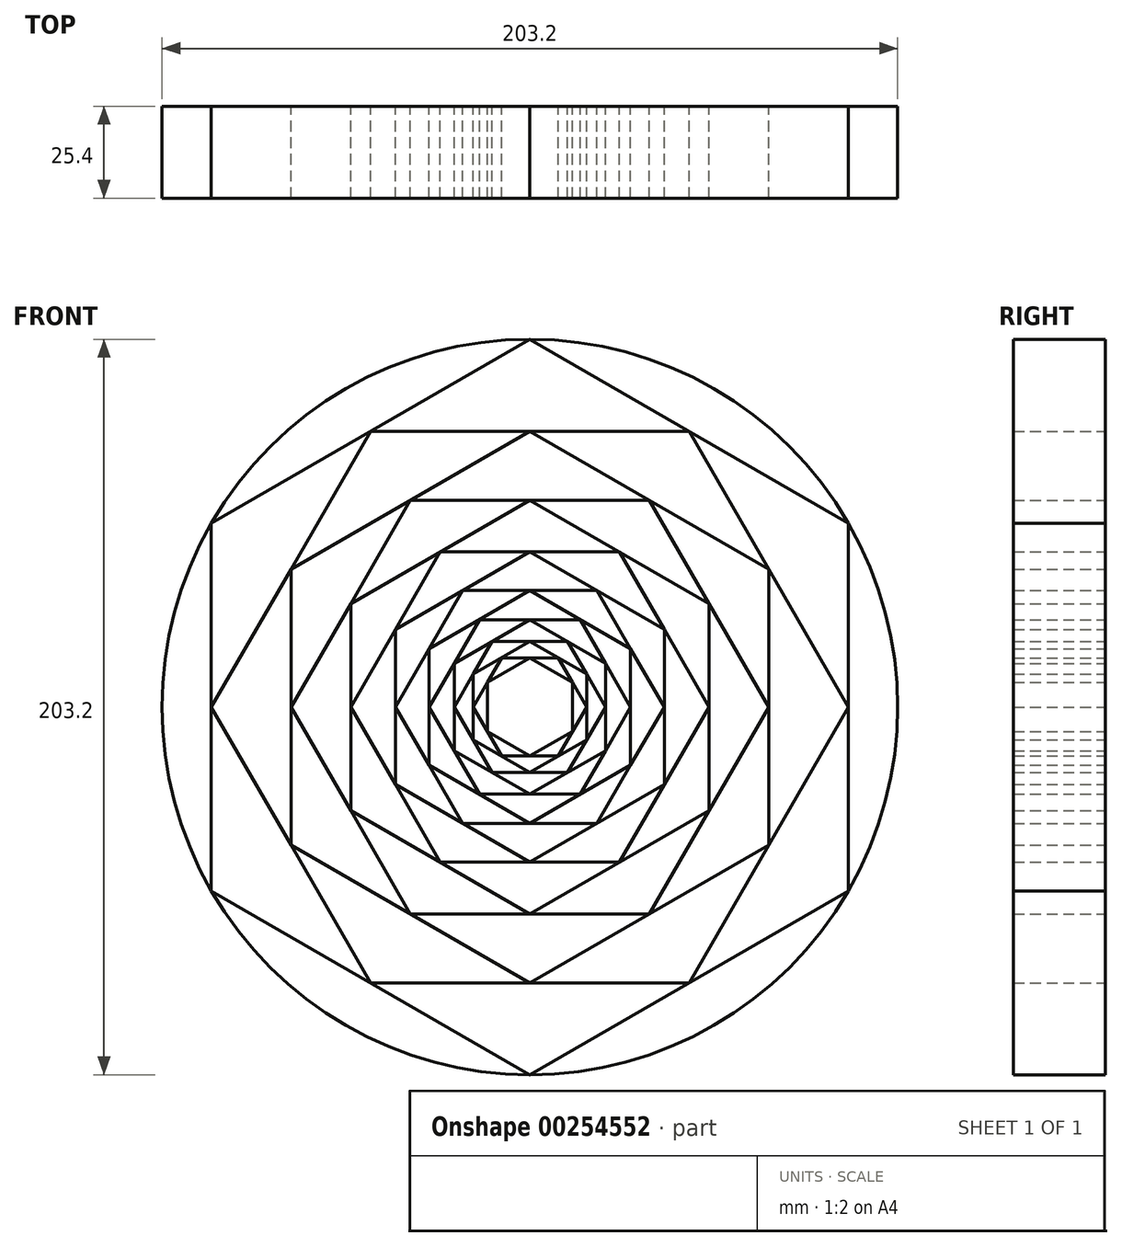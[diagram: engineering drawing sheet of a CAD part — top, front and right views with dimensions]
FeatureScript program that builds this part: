
annotation { "Feature Type Name" : "Feature", "Feature Type Description" : "" }
export const myFeature = defineFeature(function(context is Context, id is Id, definition is map)
    precondition{}
    {
        {
            var Q0;
            Q0=qCreatedBy(makeId("Front.planeOp"),FACE);
            var sketch = newSketch(context, id + "F0", { "sketchPlane" : qUnion([Q0])});
            skCircle(sketch, "E0", {"center": v(0, 0) * mm, "radius": 101.6 * mm});
            skCircle(sketch, "E1.cCircle", {"center": v(0, 0) * mm, "radius": 101.6 * mm, "construction": true});
            skLineSegment(sketch, "E1.0", {"start": v(0, 101.6) * mm, "end": v(87.99, 50.8) * mm});
            skLineSegment(sketch, "E1.1", {"start": v(87.99, 50.8) * mm, "end": v(87.99, -50.8) * mm});
            skLineSegment(sketch, "E1.2", {"start": v(87.99, -50.8) * mm, "end": v(0, -101.6) * mm});
            skLineSegment(sketch, "E1.3", {"start": v(0, -101.6) * mm, "end": v(-87.99, -50.8) * mm});
            skLineSegment(sketch, "E1.4", {"start": v(-87.99, -50.8) * mm, "end": v(-87.99, 50.8) * mm});
            skLineSegment(sketch, "E1.5", {"start": v(-87.99, 50.8) * mm, "end": v(0, 101.6) * mm});
            skCircle(sketch, "E2.cCircle", {"center": v(0, 0) * mm, "radius": 87.99 * mm, "construction": true});
            skLineSegment(sketch, "E2.0", {"start": v(-87.99, 0) * mm, "end": v(-44, 76.2) * mm});
            skLineSegment(sketch, "E2.1", {"start": v(-44, 76.2) * mm, "end": v(44, 76.2) * mm});
            skLineSegment(sketch, "E2.2", {"start": v(44, 76.2) * mm, "end": v(87.99, 0) * mm});
            skLineSegment(sketch, "E2.3", {"start": v(87.99, 0) * mm, "end": v(44, -76.2) * mm});
            skLineSegment(sketch, "E2.4", {"start": v(44, -76.2) * mm, "end": v(-44, -76.2) * mm});
            skLineSegment(sketch, "E2.5", {"start": v(-44, -76.2) * mm, "end": v(-87.99, 0) * mm});
            skCircle(sketch, "E3.cCircle", {"center": v(0, 0) * mm, "radius": 76.2 * mm, "construction": true});
            skLineSegment(sketch, "E3.0", {"start": v(0, 76.2) * mm, "end": v(66, 38.1) * mm});
            skLineSegment(sketch, "E3.1", {"start": v(66, 38.1) * mm, "end": v(66, -38.1) * mm});
            skLineSegment(sketch, "E3.2", {"start": v(66, -38.1) * mm, "end": v(0, -76.2) * mm});
            skLineSegment(sketch, "E3.3", {"start": v(0, -76.2) * mm, "end": v(-66, -38.1) * mm});
            skLineSegment(sketch, "E3.4", {"start": v(-66, -38.1) * mm, "end": v(-66, 38.1) * mm});
            skLineSegment(sketch, "E3.5", {"start": v(-66, 38.1) * mm, "end": v(0, 76.2) * mm});
            skCircle(sketch, "E4.cCircle", {"center": v(0, 0) * mm, "radius": 66 * mm, "construction": true});
            skLineSegment(sketch, "E4.0", {"start": v(66, 0) * mm, "end": v(33, -57.15) * mm});
            skLineSegment(sketch, "E4.1", {"start": v(33, -57.15) * mm, "end": v(-33, -57.15) * mm});
            skLineSegment(sketch, "E4.2", {"start": v(-33, -57.15) * mm, "end": v(-66, 0) * mm});
            skLineSegment(sketch, "E4.3", {"start": v(-66, 0) * mm, "end": v(-33, 57.15) * mm});
            skLineSegment(sketch, "E4.4", {"start": v(-33, 57.15) * mm, "end": v(33, 57.15) * mm});
            skLineSegment(sketch, "E4.5", {"start": v(33, 57.15) * mm, "end": v(66, 0) * mm});
            skCircle(sketch, "E5.cCircle", {"center": v(0, 0) * mm, "radius": 57.15 * mm, "construction": true});
            skLineSegment(sketch, "E5.0", {"start": v(0, 57.15) * mm, "end": v(49.5, 28.58) * mm});
            skLineSegment(sketch, "E5.1", {"start": v(49.5, 28.58) * mm, "end": v(49.5, -28.57) * mm});
            skLineSegment(sketch, "E5.2", {"start": v(49.5, -28.57) * mm, "end": v(0, -57.15) * mm});
            skLineSegment(sketch, "E5.3", {"start": v(0, -57.15) * mm, "end": v(-49.5, -28.58) * mm});
            skLineSegment(sketch, "E5.4", {"start": v(-49.5, -28.58) * mm, "end": v(-49.5, 28.57) * mm});
            skLineSegment(sketch, "E5.5", {"start": v(-49.5, 28.57) * mm, "end": v(0, 57.15) * mm});
            skCircle(sketch, "E6.cCircle", {"center": v(0, 0) * mm, "radius": 49.5 * mm, "construction": true});
            skLineSegment(sketch, "E6.0", {"start": v(49.5, 0) * mm, "end": v(24.75, -42.86) * mm});
            skLineSegment(sketch, "E6.1", {"start": v(24.75, -42.86) * mm, "end": v(-24.75, -42.86) * mm});
            skLineSegment(sketch, "E6.2", {"start": v(-24.75, -42.86) * mm, "end": v(-49.5, 0) * mm});
            skLineSegment(sketch, "E6.3", {"start": v(-49.5, 0) * mm, "end": v(-24.75, 42.86) * mm});
            skLineSegment(sketch, "E6.4", {"start": v(-24.75, 42.86) * mm, "end": v(24.75, 42.86) * mm});
            skLineSegment(sketch, "E6.5", {"start": v(24.75, 42.86) * mm, "end": v(49.5, 0) * mm});
            skCircle(sketch, "E7.cCircle", {"center": v(0, 0) * mm, "radius": 42.86 * mm, "construction": true});
            skLineSegment(sketch, "E7.0", {"start": v(0, 42.86) * mm, "end": v(37.12, 21.43) * mm});
            skLineSegment(sketch, "E7.1", {"start": v(37.12, 21.43) * mm, "end": v(37.12, -21.43) * mm});
            skLineSegment(sketch, "E7.2", {"start": v(37.12, -21.43) * mm, "end": v(0, -42.86) * mm});
            skLineSegment(sketch, "E7.3", {"start": v(0, -42.86) * mm, "end": v(-37.12, -21.43) * mm});
            skLineSegment(sketch, "E7.4", {"start": v(-37.12, -21.43) * mm, "end": v(-37.12, 21.43) * mm});
            skLineSegment(sketch, "E7.5", {"start": v(-37.12, 21.43) * mm, "end": v(0, 42.86) * mm});
            skCircle(sketch, "E8.cCircle", {"center": v(0, 0) * mm, "radius": 37.12 * mm, "construction": true});
            skLineSegment(sketch, "E8.0", {"start": v(37.12, 0) * mm, "end": v(18.56, -32.15) * mm});
            skLineSegment(sketch, "E8.1", {"start": v(18.56, -32.15) * mm, "end": v(-18.56, -32.15) * mm});
            skLineSegment(sketch, "E8.2", {"start": v(-18.56, -32.15) * mm, "end": v(-37.12, 0) * mm});
            skLineSegment(sketch, "E8.3", {"start": v(-37.12, 0) * mm, "end": v(-18.56, 32.15) * mm});
            skLineSegment(sketch, "E8.4", {"start": v(-18.56, 32.15) * mm, "end": v(18.56, 32.15) * mm});
            skLineSegment(sketch, "E8.5", {"start": v(18.56, 32.15) * mm, "end": v(37.12, 0) * mm});
            skCircle(sketch, "E9.cCircle", {"center": v(0, 0) * mm, "radius": 32.15 * mm, "construction": true});
            skLineSegment(sketch, "E9.0", {"start": v(0, 32.15) * mm, "end": v(27.84, 16.07) * mm});
            skLineSegment(sketch, "E9.1", {"start": v(27.84, 16.07) * mm, "end": v(27.84, -16.07) * mm});
            skLineSegment(sketch, "E9.2", {"start": v(27.84, -16.07) * mm, "end": v(0, -32.15) * mm});
            skLineSegment(sketch, "E9.3", {"start": v(0, -32.15) * mm, "end": v(-27.84, -16.07) * mm});
            skLineSegment(sketch, "E9.4", {"start": v(-27.84, -16.07) * mm, "end": v(-27.84, 16.07) * mm});
            skLineSegment(sketch, "E9.5", {"start": v(-27.84, 16.07) * mm, "end": v(0, 32.15) * mm});
            skCircle(sketch, "E10.cCircle", {"center": v(0, 0) * mm, "radius": 27.84 * mm, "construction": true});
            skLineSegment(sketch, "E10.0", {"start": v(27.84, 0) * mm, "end": v(13.92, -24.11) * mm});
            skLineSegment(sketch, "E10.1", {"start": v(13.92, -24.11) * mm, "end": v(-13.92, -24.11) * mm});
            skLineSegment(sketch, "E10.2", {"start": v(-13.92, -24.11) * mm, "end": v(-27.84, 0) * mm});
            skLineSegment(sketch, "E10.3", {"start": v(-27.84, 0) * mm, "end": v(-13.92, 24.11) * mm});
            skLineSegment(sketch, "E10.4", {"start": v(-13.92, 24.11) * mm, "end": v(13.92, 24.11) * mm});
            skLineSegment(sketch, "E10.5", {"start": v(13.92, 24.11) * mm, "end": v(27.84, 0) * mm});
            skCircle(sketch, "E11.cCircle", {"center": v(0, 0) * mm, "radius": 24.11 * mm, "construction": true});
            skLineSegment(sketch, "E11.0", {"start": v(0, 24.11) * mm, "end": v(20.88, 12.06) * mm});
            skLineSegment(sketch, "E11.1", {"start": v(20.88, 12.06) * mm, "end": v(20.88, -12.06) * mm});
            skLineSegment(sketch, "E11.2", {"start": v(20.88, -12.06) * mm, "end": v(0, -24.11) * mm});
            skLineSegment(sketch, "E11.3", {"start": v(0, -24.11) * mm, "end": v(-20.88, -12.06) * mm});
            skLineSegment(sketch, "E11.4", {"start": v(-20.88, -12.06) * mm, "end": v(-20.88, 12.06) * mm});
            skLineSegment(sketch, "E11.5", {"start": v(-20.88, 12.06) * mm, "end": v(0, 24.11) * mm});
            skCircle(sketch, "E12.cCircle", {"center": v(0, 0) * mm, "radius": 20.88 * mm, "construction": true});
            skLineSegment(sketch, "E13.0", {"start": v(20.88, 0) * mm, "end": v(10.44, -18.08) * mm});
            skLineSegment(sketch, "E13.1", {"start": v(10.44, -18.08) * mm, "end": v(-10.44, -18.08) * mm});
            skLineSegment(sketch, "E13.2", {"start": v(-10.44, -18.08) * mm, "end": v(-20.88, 0) * mm});
            skLineSegment(sketch, "E13.3", {"start": v(-20.88, 0) * mm, "end": v(-10.44, 18.08) * mm});
            skLineSegment(sketch, "E13.4", {"start": v(-10.44, 18.08) * mm, "end": v(10.44, 18.08) * mm});
            skLineSegment(sketch, "E13.5", {"start": v(10.44, 18.08) * mm, "end": v(20.88, 0) * mm});
            skCircle(sketch, "E14.cCircle", {"center": v(0, 0) * mm, "radius": 18.08 * mm, "construction": true});
            skLineSegment(sketch, "E14.0", {"start": v(0, 18.08) * mm, "end": v(15.66, 9.04) * mm});
            skLineSegment(sketch, "E14.1", {"start": v(15.66, 9.04) * mm, "end": v(15.66, -9.04) * mm});
            skLineSegment(sketch, "E14.2", {"start": v(15.66, -9.04) * mm, "end": v(0, -18.08) * mm});
            skLineSegment(sketch, "E14.3", {"start": v(0, -18.08) * mm, "end": v(-15.66, -9.04) * mm});
            skLineSegment(sketch, "E14.4", {"start": v(-15.66, -9.04) * mm, "end": v(-15.66, 9.04) * mm});
            skLineSegment(sketch, "E14.5", {"start": v(-15.66, 9.04) * mm, "end": v(0, 18.08) * mm});
            skCircle(sketch, "E15.cCircle", {"center": v(0, 0) * mm, "radius": 15.66 * mm, "construction": true});
            skLineSegment(sketch, "E15.0", {"start": v(15.66, 0) * mm, "end": v(7.83, -13.56) * mm});
            skLineSegment(sketch, "E15.1", {"start": v(7.83, -13.56) * mm, "end": v(-7.83, -13.56) * mm});
            skLineSegment(sketch, "E15.2", {"start": v(-7.83, -13.56) * mm, "end": v(-15.66, 0) * mm});
            skLineSegment(sketch, "E15.3", {"start": v(-15.66, 0) * mm, "end": v(-7.83, 13.56) * mm});
            skLineSegment(sketch, "E15.4", {"start": v(-7.83, 13.56) * mm, "end": v(7.83, 13.56) * mm});
            skLineSegment(sketch, "E15.5", {"start": v(7.83, 13.56) * mm, "end": v(15.66, 0) * mm});
            skCircle(sketch, "E16.cCircle", {"center": v(0, 0) * mm, "radius": 13.56 * mm, "construction": true});
            skLineSegment(sketch, "E16.0", {"start": v(0, 13.56) * mm, "end": v(11.75, 6.78) * mm});
            skLineSegment(sketch, "E16.1", {"start": v(11.75, 6.78) * mm, "end": v(11.75, -6.78) * mm});
            skLineSegment(sketch, "E16.2", {"start": v(11.75, -6.78) * mm, "end": v(0, -13.56) * mm});
            skLineSegment(sketch, "E16.3", {"start": v(0, -13.56) * mm, "end": v(-11.75, -6.78) * mm});
            skLineSegment(sketch, "E16.4", {"start": v(-11.75, -6.78) * mm, "end": v(-11.75, 6.78) * mm});
            skLineSegment(sketch, "E16.5", {"start": v(-11.75, 6.78) * mm, "end": v(0, 13.56) * mm});
            skCircle(sketch, "E17.cCircle", {"center": v(0, 0) * mm, "radius": 11.75 * mm, "construction": true});
            skLineSegment(sketch, "E17.0", {"start": v(11.75, 0) * mm, "end": v(5.87, -10.17) * mm});
            skLineSegment(sketch, "E17.1", {"start": v(5.87, -10.17) * mm, "end": v(-5.87, -10.17) * mm});
            skLineSegment(sketch, "E17.2", {"start": v(-5.87, -10.17) * mm, "end": v(-11.75, 0) * mm});
            skLineSegment(sketch, "E17.3", {"start": v(-11.75, 0) * mm, "end": v(-5.87, 10.17) * mm});
            skLineSegment(sketch, "E17.4", {"start": v(-5.87, 10.17) * mm, "end": v(5.87, 10.17) * mm});
            skLineSegment(sketch, "E17.5", {"start": v(5.87, 10.17) * mm, "end": v(11.75, 0) * mm});
            skSolve(sketch);
        }
        {
            var Q0;
            {var subQ0=sQuery(id+"F0.wireOp",EDGE,"E1.5");var subQ1=sQuery(id+"F0.wireOp",EDGE,"E0");var subQ2=makeQuery(id+"F0.imprint","INTERSECT",VERTEX,{"derivedFrom":[subQ1,sQuery(id+"F0.wireOp",EDGE,"E1.0"),subQ0]});Q0=makeQuery(id+"F0.imprint","IMPRINT",FACE,{"disambiguationData":[TD([[makeQuery(id+"F0.imprint","IMPRINT",EDGE,{"disambiguationData":[TD([[subQ2,-1.0]])],"derivedFrom":subQ1}),1.0]])]});}
            var Q1;
            {var subQ0=sQuery(id+"F0.wireOp",EDGE,"E1.0");var subQ1=sQuery(id+"F0.wireOp",EDGE,"E0");var subQ2=makeQuery(id+"F0.imprint","INTERSECT",VERTEX,{"derivedFrom":[subQ1,subQ0,sQuery(id+"F0.wireOp",EDGE,"E1.5")]});Q1=makeQuery(id+"F0.imprint","IMPRINT",FACE,{"disambiguationData":[TD([[makeQuery(id+"F0.imprint","IMPRINT",EDGE,{"disambiguationData":[TD([[subQ2,1.0]])],"derivedFrom":subQ1}),1.0]])]});}
            var Q2;
            {var subQ0=sQuery(id+"F0.wireOp",EDGE,"E1.1");var subQ1=sQuery(id+"F0.wireOp",EDGE,"E0");var subQ2=makeQuery(id+"F0.imprint","INTERSECT",VERTEX,{"derivedFrom":[subQ1,sQuery(id+"F0.wireOp",EDGE,"E1.0"),subQ0]});Q2=makeQuery(id+"F0.imprint","IMPRINT",FACE,{"disambiguationData":[TD([[makeQuery(id+"F0.imprint","IMPRINT",EDGE,{"disambiguationData":[TD([[subQ2,1.0]])],"derivedFrom":subQ1}),1.0]])]});}
            var Q3;
            {var subQ0=sQuery(id+"F0.wireOp",EDGE,"E1.2");var subQ1=sQuery(id+"F0.wireOp",EDGE,"E0");var subQ2=makeQuery(id+"F0.imprint","INTERSECT",VERTEX,{"derivedFrom":[subQ1,sQuery(id+"F0.wireOp",EDGE,"E1.1"),subQ0]});Q3=makeQuery(id+"F0.imprint","IMPRINT",FACE,{"disambiguationData":[TD([[makeQuery(id+"F0.imprint","IMPRINT",EDGE,{"disambiguationData":[TD([[subQ2,1.0]])],"derivedFrom":subQ1}),1.0]])]});}
            var Q4;
            {var subQ0=sQuery(id+"F0.wireOp",EDGE,"E1.3");var subQ1=sQuery(id+"F0.wireOp",EDGE,"E0");var subQ2=makeQuery(id+"F0.imprint","INTERSECT",VERTEX,{"derivedFrom":[subQ1,sQuery(id+"F0.wireOp",EDGE,"E1.2"),subQ0]});Q4=makeQuery(id+"F0.imprint","IMPRINT",FACE,{"disambiguationData":[TD([[makeQuery(id+"F0.imprint","IMPRINT",EDGE,{"disambiguationData":[TD([[subQ2,1.0]])],"derivedFrom":subQ1}),1.0]])]});}
            var Q5;
            {var subQ0=sQuery(id+"F0.wireOp",EDGE,"E1.4");var subQ1=sQuery(id+"F0.wireOp",EDGE,"E0");var subQ2=makeQuery(id+"F0.imprint","INTERSECT",VERTEX,{"derivedFrom":[subQ1,sQuery(id+"F0.wireOp",EDGE,"E1.3"),subQ0]});Q5=makeQuery(id+"F0.imprint","IMPRINT",FACE,{"disambiguationData":[TD([[makeQuery(id+"F0.imprint","IMPRINT",EDGE,{"disambiguationData":[TD([[subQ2,1.0]])],"derivedFrom":subQ1}),1.0]])]});}
            var Q6;
            {var subQ0=sQuery(id+"F0.wireOp",EDGE,"E2.5");var subQ1=sQuery(id+"F0.wireOp",EDGE,"E2.4");var subQ2=makeQuery(id+"F0.imprint","INTERSECT",VERTEX,{"derivedFrom":[sQuery(id+"F0.wireOp",EDGE,"E1.3"),subQ1,subQ0]});Q6=makeQuery(id+"F0.imprint","IMPRINT",FACE,{"disambiguationData":[TD([[makeQuery(id+"F0.imprint","IMPRINT",EDGE,{"disambiguationData":[TD([[subQ2,1.0]])],"derivedFrom":subQ1}),-1.0]])]});}
            var Q7;
            {var subQ0=sQuery(id+"F0.wireOp",EDGE,"E2.4");var subQ1=sQuery(id+"F0.wireOp",EDGE,"E2.3");var subQ2=makeQuery(id+"F0.imprint","INTERSECT",VERTEX,{"derivedFrom":[sQuery(id+"F0.wireOp",EDGE,"E1.2"),subQ1,subQ0]});Q7=makeQuery(id+"F0.imprint","IMPRINT",FACE,{"disambiguationData":[TD([[makeQuery(id+"F0.imprint","IMPRINT",EDGE,{"disambiguationData":[TD([[subQ2,1.0]])],"derivedFrom":subQ1}),-1.0]])]});}
            var Q8;
            {var subQ0=sQuery(id+"F0.wireOp",EDGE,"E2.3");var subQ1=sQuery(id+"F0.wireOp",EDGE,"E2.2");var subQ2=makeQuery(id+"F0.imprint","INTERSECT",VERTEX,{"derivedFrom":[sQuery(id+"F0.wireOp",EDGE,"E1.1"),subQ1,subQ0]});Q8=makeQuery(id+"F0.imprint","IMPRINT",FACE,{"disambiguationData":[TD([[makeQuery(id+"F0.imprint","IMPRINT",EDGE,{"disambiguationData":[TD([[subQ2,1.0]])],"derivedFrom":subQ1}),-1.0]])]});}
            var Q9;
            {var subQ0=sQuery(id+"F0.wireOp",EDGE,"E2.2");var subQ1=sQuery(id+"F0.wireOp",EDGE,"E2.1");var subQ2=makeQuery(id+"F0.imprint","INTERSECT",VERTEX,{"derivedFrom":[sQuery(id+"F0.wireOp",EDGE,"E1.0"),subQ1,subQ0]});Q9=makeQuery(id+"F0.imprint","IMPRINT",FACE,{"disambiguationData":[TD([[makeQuery(id+"F0.imprint","IMPRINT",EDGE,{"disambiguationData":[TD([[subQ2,1.0]])],"derivedFrom":subQ1}),-1.0]])]});}
            var Q10;
            {var subQ0=sQuery(id+"F0.wireOp",EDGE,"E2.1");var subQ1=sQuery(id+"F0.wireOp",EDGE,"E2.0");var subQ2=makeQuery(id+"F0.imprint","INTERSECT",VERTEX,{"derivedFrom":[sQuery(id+"F0.wireOp",EDGE,"E1.5"),subQ1,subQ0]});Q10=makeQuery(id+"F0.imprint","IMPRINT",FACE,{"disambiguationData":[TD([[makeQuery(id+"F0.imprint","IMPRINT",EDGE,{"disambiguationData":[TD([[subQ2,1.0]])],"derivedFrom":subQ1}),-1.0]])]});}
            var Q11;
            {var subQ0=sQuery(id+"F0.wireOp",EDGE,"E2.5");var subQ1=sQuery(id+"F0.wireOp",EDGE,"E2.0");var subQ2=makeQuery(id+"F0.imprint","INTERSECT",VERTEX,{"derivedFrom":[sQuery(id+"F0.wireOp",EDGE,"E1.4"),subQ1,subQ0]});Q11=makeQuery(id+"F0.imprint","IMPRINT",FACE,{"disambiguationData":[TD([[makeQuery(id+"F0.imprint","IMPRINT",EDGE,{"disambiguationData":[TD([[subQ2,-1.0]])],"derivedFrom":subQ1}),-1.0]])]});}
            var Q12;
            {var subQ0=sQuery(id+"F0.wireOp",EDGE,"E4.3");var subQ1=sQuery(id+"F0.wireOp",EDGE,"E4.2");var subQ2=makeQuery(id+"F0.imprint","INTERSECT",VERTEX,{"derivedFrom":[sQuery(id+"F0.wireOp",EDGE,"E3.4"),subQ1,subQ0]});Q12=makeQuery(id+"F0.imprint","IMPRINT",FACE,{"disambiguationData":[TD([[makeQuery(id+"F0.imprint","IMPRINT",EDGE,{"disambiguationData":[TD([[subQ2,1.0]])],"derivedFrom":subQ1}),-1.0]])]});}
            var Q13;
            {var subQ0=sQuery(id+"F0.wireOp",EDGE,"E4.2");var subQ1=sQuery(id+"F0.wireOp",EDGE,"E4.1");var subQ2=makeQuery(id+"F0.imprint","INTERSECT",VERTEX,{"derivedFrom":[sQuery(id+"F0.wireOp",EDGE,"E3.3"),subQ1,subQ0]});Q13=makeQuery(id+"F0.imprint","IMPRINT",FACE,{"disambiguationData":[TD([[makeQuery(id+"F0.imprint","IMPRINT",EDGE,{"disambiguationData":[TD([[subQ2,1.0]])],"derivedFrom":subQ1}),-1.0]])]});}
            var Q14;
            {var subQ0=sQuery(id+"F0.wireOp",EDGE,"E4.1");var subQ1=sQuery(id+"F0.wireOp",EDGE,"E4.0");var subQ2=makeQuery(id+"F0.imprint","INTERSECT",VERTEX,{"derivedFrom":[sQuery(id+"F0.wireOp",EDGE,"E3.2"),subQ1,subQ0]});Q14=makeQuery(id+"F0.imprint","IMPRINT",FACE,{"disambiguationData":[TD([[makeQuery(id+"F0.imprint","IMPRINT",EDGE,{"disambiguationData":[TD([[subQ2,1.0]])],"derivedFrom":subQ1}),-1.0]])]});}
            var Q15;
            {var subQ0=sQuery(id+"F0.wireOp",EDGE,"E4.5");var subQ1=sQuery(id+"F0.wireOp",EDGE,"E4.0");var subQ2=makeQuery(id+"F0.imprint","INTERSECT",VERTEX,{"derivedFrom":[sQuery(id+"F0.wireOp",EDGE,"E3.1"),subQ1,subQ0]});Q15=makeQuery(id+"F0.imprint","IMPRINT",FACE,{"disambiguationData":[TD([[makeQuery(id+"F0.imprint","IMPRINT",EDGE,{"disambiguationData":[TD([[subQ2,-1.0]])],"derivedFrom":subQ1}),-1.0]])]});}
            var Q16;
            {var subQ0=sQuery(id+"F0.wireOp",EDGE,"E4.5");var subQ1=sQuery(id+"F0.wireOp",EDGE,"E4.4");var subQ2=makeQuery(id+"F0.imprint","INTERSECT",VERTEX,{"derivedFrom":[sQuery(id+"F0.wireOp",EDGE,"E3.0"),subQ1,subQ0]});Q16=makeQuery(id+"F0.imprint","IMPRINT",FACE,{"disambiguationData":[TD([[makeQuery(id+"F0.imprint","IMPRINT",EDGE,{"disambiguationData":[TD([[subQ2,1.0]])],"derivedFrom":subQ1}),-1.0]])]});}
            var Q17;
            {var subQ0=sQuery(id+"F0.wireOp",EDGE,"E4.4");var subQ1=sQuery(id+"F0.wireOp",EDGE,"E4.3");var subQ2=makeQuery(id+"F0.imprint","INTERSECT",VERTEX,{"derivedFrom":[sQuery(id+"F0.wireOp",EDGE,"E3.5"),subQ1,subQ0]});Q17=makeQuery(id+"F0.imprint","IMPRINT",FACE,{"disambiguationData":[TD([[makeQuery(id+"F0.imprint","IMPRINT",EDGE,{"disambiguationData":[TD([[subQ2,1.0]])],"derivedFrom":subQ1}),-1.0]])]});}
            var Q18;
            {var subQ0=sQuery(id+"F0.wireOp",EDGE,"E6.4");var subQ1=sQuery(id+"F0.wireOp",EDGE,"E6.3");var subQ2=makeQuery(id+"F0.imprint","INTERSECT",VERTEX,{"derivedFrom":[sQuery(id+"F0.wireOp",EDGE,"E5.5"),subQ1,subQ0]});Q18=makeQuery(id+"F0.imprint","IMPRINT",FACE,{"disambiguationData":[TD([[makeQuery(id+"F0.imprint","IMPRINT",EDGE,{"disambiguationData":[TD([[subQ2,1.0]])],"derivedFrom":subQ1}),-1.0]])]});}
            var Q19;
            {var subQ0=sQuery(id+"F0.wireOp",EDGE,"E6.3");var subQ1=sQuery(id+"F0.wireOp",EDGE,"E6.2");var subQ2=makeQuery(id+"F0.imprint","INTERSECT",VERTEX,{"derivedFrom":[sQuery(id+"F0.wireOp",EDGE,"E5.4"),subQ1,subQ0]});Q19=makeQuery(id+"F0.imprint","IMPRINT",FACE,{"disambiguationData":[TD([[makeQuery(id+"F0.imprint","IMPRINT",EDGE,{"disambiguationData":[TD([[subQ2,1.0]])],"derivedFrom":subQ1}),-1.0]])]});}
            var Q20;
            {var subQ0=sQuery(id+"F0.wireOp",EDGE,"E6.2");var subQ1=sQuery(id+"F0.wireOp",EDGE,"E6.1");var subQ2=makeQuery(id+"F0.imprint","INTERSECT",VERTEX,{"derivedFrom":[sQuery(id+"F0.wireOp",EDGE,"E5.3"),subQ1,subQ0]});Q20=makeQuery(id+"F0.imprint","IMPRINT",FACE,{"disambiguationData":[TD([[makeQuery(id+"F0.imprint","IMPRINT",EDGE,{"disambiguationData":[TD([[subQ2,1.0]])],"derivedFrom":subQ1}),-1.0]])]});}
            var Q21;
            {var subQ0=sQuery(id+"F0.wireOp",EDGE,"E6.1");var subQ1=sQuery(id+"F0.wireOp",EDGE,"E6.0");var subQ2=makeQuery(id+"F0.imprint","INTERSECT",VERTEX,{"derivedFrom":[sQuery(id+"F0.wireOp",EDGE,"E5.2"),subQ1,subQ0]});Q21=makeQuery(id+"F0.imprint","IMPRINT",FACE,{"disambiguationData":[TD([[makeQuery(id+"F0.imprint","IMPRINT",EDGE,{"disambiguationData":[TD([[subQ2,1.0]])],"derivedFrom":subQ1}),-1.0]])]});}
            var Q22;
            {var subQ0=sQuery(id+"F0.wireOp",EDGE,"E6.5");var subQ1=sQuery(id+"F0.wireOp",EDGE,"E6.0");var subQ2=makeQuery(id+"F0.imprint","INTERSECT",VERTEX,{"derivedFrom":[sQuery(id+"F0.wireOp",EDGE,"E5.1"),subQ1,subQ0]});Q22=makeQuery(id+"F0.imprint","IMPRINT",FACE,{"disambiguationData":[TD([[makeQuery(id+"F0.imprint","IMPRINT",EDGE,{"disambiguationData":[TD([[subQ2,-1.0]])],"derivedFrom":subQ1}),-1.0]])]});}
            var Q23;
            {var subQ0=sQuery(id+"F0.wireOp",EDGE,"E6.5");var subQ1=sQuery(id+"F0.wireOp",EDGE,"E6.4");var subQ2=makeQuery(id+"F0.imprint","INTERSECT",VERTEX,{"derivedFrom":[sQuery(id+"F0.wireOp",EDGE,"E5.0"),subQ1,subQ0]});Q23=makeQuery(id+"F0.imprint","IMPRINT",FACE,{"disambiguationData":[TD([[makeQuery(id+"F0.imprint","IMPRINT",EDGE,{"disambiguationData":[TD([[subQ2,1.0]])],"derivedFrom":subQ1}),-1.0]])]});}
            var Q24;
            {var subQ0=sQuery(id+"F0.wireOp",EDGE,"E8.5");var subQ1=sQuery(id+"F0.wireOp",EDGE,"E8.4");var subQ2=makeQuery(id+"F0.imprint","INTERSECT",VERTEX,{"derivedFrom":[sQuery(id+"F0.wireOp",EDGE,"E7.0"),subQ1,subQ0]});Q24=makeQuery(id+"F0.imprint","IMPRINT",FACE,{"disambiguationData":[TD([[makeQuery(id+"F0.imprint","IMPRINT",EDGE,{"disambiguationData":[TD([[subQ2,1.0]])],"derivedFrom":subQ1}),-1.0]])]});}
            var Q25;
            {var subQ0=sQuery(id+"F0.wireOp",EDGE,"E8.4");var subQ1=sQuery(id+"F0.wireOp",EDGE,"E8.3");var subQ2=makeQuery(id+"F0.imprint","INTERSECT",VERTEX,{"derivedFrom":[sQuery(id+"F0.wireOp",EDGE,"E7.5"),subQ1,subQ0]});Q25=makeQuery(id+"F0.imprint","IMPRINT",FACE,{"disambiguationData":[TD([[makeQuery(id+"F0.imprint","IMPRINT",EDGE,{"disambiguationData":[TD([[subQ2,1.0]])],"derivedFrom":subQ1}),-1.0]])]});}
            var Q26;
            {var subQ0=sQuery(id+"F0.wireOp",EDGE,"E8.3");var subQ1=sQuery(id+"F0.wireOp",EDGE,"E8.2");var subQ2=makeQuery(id+"F0.imprint","INTERSECT",VERTEX,{"derivedFrom":[sQuery(id+"F0.wireOp",EDGE,"E7.4"),subQ1,subQ0]});Q26=makeQuery(id+"F0.imprint","IMPRINT",FACE,{"disambiguationData":[TD([[makeQuery(id+"F0.imprint","IMPRINT",EDGE,{"disambiguationData":[TD([[subQ2,1.0]])],"derivedFrom":subQ1}),-1.0]])]});}
            var Q27;
            {var subQ0=sQuery(id+"F0.wireOp",EDGE,"E8.2");var subQ1=sQuery(id+"F0.wireOp",EDGE,"E8.1");var subQ2=makeQuery(id+"F0.imprint","INTERSECT",VERTEX,{"derivedFrom":[sQuery(id+"F0.wireOp",EDGE,"E7.3"),subQ1,subQ0]});Q27=makeQuery(id+"F0.imprint","IMPRINT",FACE,{"disambiguationData":[TD([[makeQuery(id+"F0.imprint","IMPRINT",EDGE,{"disambiguationData":[TD([[subQ2,1.0]])],"derivedFrom":subQ1}),-1.0]])]});}
            var Q28;
            {var subQ0=sQuery(id+"F0.wireOp",EDGE,"E8.1");var subQ1=sQuery(id+"F0.wireOp",EDGE,"E8.0");var subQ2=makeQuery(id+"F0.imprint","INTERSECT",VERTEX,{"derivedFrom":[sQuery(id+"F0.wireOp",EDGE,"E7.2"),subQ1,subQ0]});Q28=makeQuery(id+"F0.imprint","IMPRINT",FACE,{"disambiguationData":[TD([[makeQuery(id+"F0.imprint","IMPRINT",EDGE,{"disambiguationData":[TD([[subQ2,1.0]])],"derivedFrom":subQ1}),-1.0]])]});}
            var Q29;
            {var subQ0=sQuery(id+"F0.wireOp",EDGE,"E8.5");var subQ1=sQuery(id+"F0.wireOp",EDGE,"E8.0");var subQ2=makeQuery(id+"F0.imprint","INTERSECT",VERTEX,{"derivedFrom":[sQuery(id+"F0.wireOp",EDGE,"E7.1"),subQ1,subQ0]});Q29=makeQuery(id+"F0.imprint","IMPRINT",FACE,{"disambiguationData":[TD([[makeQuery(id+"F0.imprint","IMPRINT",EDGE,{"disambiguationData":[TD([[subQ2,-1.0]])],"derivedFrom":subQ1}),-1.0]])]});}
            var Q30;
            {var subQ0=sQuery(id+"F0.wireOp",EDGE,"E10.5");var subQ1=sQuery(id+"F0.wireOp",EDGE,"E10.4");var subQ2=makeQuery(id+"F0.imprint","INTERSECT",VERTEX,{"derivedFrom":[sQuery(id+"F0.wireOp",EDGE,"E9.0"),subQ1,subQ0]});Q30=makeQuery(id+"F0.imprint","IMPRINT",FACE,{"disambiguationData":[TD([[makeQuery(id+"F0.imprint","IMPRINT",EDGE,{"disambiguationData":[TD([[subQ2,1.0]])],"derivedFrom":subQ1}),-1.0]])]});}
            var Q31;
            {var subQ0=sQuery(id+"F0.wireOp",EDGE,"E10.4");var subQ1=sQuery(id+"F0.wireOp",EDGE,"E10.3");var subQ2=makeQuery(id+"F0.imprint","INTERSECT",VERTEX,{"derivedFrom":[sQuery(id+"F0.wireOp",EDGE,"E9.5"),subQ1,subQ0]});Q31=makeQuery(id+"F0.imprint","IMPRINT",FACE,{"disambiguationData":[TD([[makeQuery(id+"F0.imprint","IMPRINT",EDGE,{"disambiguationData":[TD([[subQ2,1.0]])],"derivedFrom":subQ1}),-1.0]])]});}
            var Q32;
            {var subQ0=sQuery(id+"F0.wireOp",EDGE,"E10.3");var subQ1=sQuery(id+"F0.wireOp",EDGE,"E10.2");var subQ2=makeQuery(id+"F0.imprint","INTERSECT",VERTEX,{"derivedFrom":[sQuery(id+"F0.wireOp",EDGE,"E9.4"),subQ1,subQ0]});Q32=makeQuery(id+"F0.imprint","IMPRINT",FACE,{"disambiguationData":[TD([[makeQuery(id+"F0.imprint","IMPRINT",EDGE,{"disambiguationData":[TD([[subQ2,1.0]])],"derivedFrom":subQ1}),-1.0]])]});}
            var Q33;
            {var subQ0=sQuery(id+"F0.wireOp",EDGE,"E10.2");var subQ1=sQuery(id+"F0.wireOp",EDGE,"E10.1");var subQ2=makeQuery(id+"F0.imprint","INTERSECT",VERTEX,{"derivedFrom":[sQuery(id+"F0.wireOp",EDGE,"E9.3"),subQ1,subQ0]});Q33=makeQuery(id+"F0.imprint","IMPRINT",FACE,{"disambiguationData":[TD([[makeQuery(id+"F0.imprint","IMPRINT",EDGE,{"disambiguationData":[TD([[subQ2,1.0]])],"derivedFrom":subQ1}),-1.0]])]});}
            var Q34;
            {var subQ0=sQuery(id+"F0.wireOp",EDGE,"E10.1");var subQ1=sQuery(id+"F0.wireOp",EDGE,"E10.0");var subQ2=makeQuery(id+"F0.imprint","INTERSECT",VERTEX,{"derivedFrom":[sQuery(id+"F0.wireOp",EDGE,"E9.2"),subQ1,subQ0]});Q34=makeQuery(id+"F0.imprint","IMPRINT",FACE,{"disambiguationData":[TD([[makeQuery(id+"F0.imprint","IMPRINT",EDGE,{"disambiguationData":[TD([[subQ2,1.0]])],"derivedFrom":subQ1}),-1.0]])]});}
            var Q35;
            {var subQ0=sQuery(id+"F0.wireOp",EDGE,"E10.5");var subQ1=sQuery(id+"F0.wireOp",EDGE,"E10.0");var subQ2=makeQuery(id+"F0.imprint","INTERSECT",VERTEX,{"derivedFrom":[sQuery(id+"F0.wireOp",EDGE,"E9.1"),subQ1,subQ0]});Q35=makeQuery(id+"F0.imprint","IMPRINT",FACE,{"disambiguationData":[TD([[makeQuery(id+"F0.imprint","IMPRINT",EDGE,{"disambiguationData":[TD([[subQ2,-1.0]])],"derivedFrom":subQ1}),-1.0]])]});}
            var Q36;
            {var subQ0=sQuery(id+"F0.wireOp",EDGE,"E13.5");var subQ1=sQuery(id+"F0.wireOp",EDGE,"E13.0");var subQ2=makeQuery(id+"F0.imprint","INTERSECT",VERTEX,{"derivedFrom":[sQuery(id+"F0.wireOp",EDGE,"E11.1"),subQ1,subQ0]});Q36=makeQuery(id+"F0.imprint","IMPRINT",FACE,{"disambiguationData":[TD([[makeQuery(id+"F0.imprint","IMPRINT",EDGE,{"disambiguationData":[TD([[subQ2,-1.0]])],"derivedFrom":subQ1}),-1.0]])]});}
            var Q37;
            {var subQ0=sQuery(id+"F0.wireOp",EDGE,"E13.5");var subQ1=sQuery(id+"F0.wireOp",EDGE,"E13.4");var subQ2=makeQuery(id+"F0.imprint","INTERSECT",VERTEX,{"derivedFrom":[sQuery(id+"F0.wireOp",EDGE,"E11.0"),subQ1,subQ0]});Q37=makeQuery(id+"F0.imprint","IMPRINT",FACE,{"disambiguationData":[TD([[makeQuery(id+"F0.imprint","IMPRINT",EDGE,{"disambiguationData":[TD([[subQ2,1.0]])],"derivedFrom":subQ1}),-1.0]])]});}
            var Q38;
            {var subQ0=sQuery(id+"F0.wireOp",EDGE,"E13.4");var subQ1=sQuery(id+"F0.wireOp",EDGE,"E13.3");var subQ2=makeQuery(id+"F0.imprint","INTERSECT",VERTEX,{"derivedFrom":[sQuery(id+"F0.wireOp",EDGE,"E11.5"),subQ1,subQ0]});Q38=makeQuery(id+"F0.imprint","IMPRINT",FACE,{"disambiguationData":[TD([[makeQuery(id+"F0.imprint","IMPRINT",EDGE,{"disambiguationData":[TD([[subQ2,1.0]])],"derivedFrom":subQ1}),-1.0]])]});}
            var Q39;
            {var subQ0=sQuery(id+"F0.wireOp",EDGE,"E13.3");var subQ1=sQuery(id+"F0.wireOp",EDGE,"E13.2");var subQ2=makeQuery(id+"F0.imprint","INTERSECT",VERTEX,{"derivedFrom":[sQuery(id+"F0.wireOp",EDGE,"E11.4"),subQ1,subQ0]});Q39=makeQuery(id+"F0.imprint","IMPRINT",FACE,{"disambiguationData":[TD([[makeQuery(id+"F0.imprint","IMPRINT",EDGE,{"disambiguationData":[TD([[subQ2,1.0]])],"derivedFrom":subQ1}),-1.0]])]});}
            var Q40;
            {var subQ0=sQuery(id+"F0.wireOp",EDGE,"E13.2");var subQ1=sQuery(id+"F0.wireOp",EDGE,"E13.1");var subQ2=makeQuery(id+"F0.imprint","INTERSECT",VERTEX,{"derivedFrom":[sQuery(id+"F0.wireOp",EDGE,"E11.3"),subQ1,subQ0]});Q40=makeQuery(id+"F0.imprint","IMPRINT",FACE,{"disambiguationData":[TD([[makeQuery(id+"F0.imprint","IMPRINT",EDGE,{"disambiguationData":[TD([[subQ2,1.0]])],"derivedFrom":subQ1}),-1.0]])]});}
            var Q41;
            {var subQ0=sQuery(id+"F0.wireOp",EDGE,"E13.1");var subQ1=sQuery(id+"F0.wireOp",EDGE,"E13.0");var subQ2=makeQuery(id+"F0.imprint","INTERSECT",VERTEX,{"derivedFrom":[sQuery(id+"F0.wireOp",EDGE,"E11.2"),subQ1,subQ0]});Q41=makeQuery(id+"F0.imprint","IMPRINT",FACE,{"disambiguationData":[TD([[makeQuery(id+"F0.imprint","IMPRINT",EDGE,{"disambiguationData":[TD([[subQ2,1.0]])],"derivedFrom":subQ1}),-1.0]])]});}
            var Q42;
            {var subQ0=sQuery(id+"F0.wireOp",EDGE,"E15.5");var subQ1=sQuery(id+"F0.wireOp",EDGE,"E15.0");var subQ2=makeQuery(id+"F0.imprint","INTERSECT",VERTEX,{"derivedFrom":[sQuery(id+"F0.wireOp",EDGE,"E14.1"),subQ1,subQ0]});Q42=makeQuery(id+"F0.imprint","IMPRINT",FACE,{"disambiguationData":[TD([[makeQuery(id+"F0.imprint","IMPRINT",EDGE,{"disambiguationData":[TD([[subQ2,-1.0]])],"derivedFrom":subQ1}),-1.0]])]});}
            var Q43;
            {var subQ0=sQuery(id+"F0.wireOp",EDGE,"E15.1");var subQ1=sQuery(id+"F0.wireOp",EDGE,"E15.0");var subQ2=makeQuery(id+"F0.imprint","INTERSECT",VERTEX,{"derivedFrom":[sQuery(id+"F0.wireOp",EDGE,"E14.2"),subQ1,subQ0]});Q43=makeQuery(id+"F0.imprint","IMPRINT",FACE,{"disambiguationData":[TD([[makeQuery(id+"F0.imprint","IMPRINT",EDGE,{"disambiguationData":[TD([[subQ2,1.0]])],"derivedFrom":subQ1}),-1.0]])]});}
            var Q44;
            {var subQ0=sQuery(id+"F0.wireOp",EDGE,"E15.5");var subQ1=sQuery(id+"F0.wireOp",EDGE,"E15.4");var subQ2=makeQuery(id+"F0.imprint","INTERSECT",VERTEX,{"derivedFrom":[sQuery(id+"F0.wireOp",EDGE,"E14.0"),subQ1,subQ0]});Q44=makeQuery(id+"F0.imprint","IMPRINT",FACE,{"disambiguationData":[TD([[makeQuery(id+"F0.imprint","IMPRINT",EDGE,{"disambiguationData":[TD([[subQ2,1.0]])],"derivedFrom":subQ1}),-1.0]])]});}
            var Q45;
            {var subQ0=sQuery(id+"F0.wireOp",EDGE,"E15.4");var subQ1=sQuery(id+"F0.wireOp",EDGE,"E15.3");var subQ2=makeQuery(id+"F0.imprint","INTERSECT",VERTEX,{"derivedFrom":[sQuery(id+"F0.wireOp",EDGE,"E14.5"),subQ1,subQ0]});Q45=makeQuery(id+"F0.imprint","IMPRINT",FACE,{"disambiguationData":[TD([[makeQuery(id+"F0.imprint","IMPRINT",EDGE,{"disambiguationData":[TD([[subQ2,1.0]])],"derivedFrom":subQ1}),-1.0]])]});}
            var Q46;
            {var subQ0=sQuery(id+"F0.wireOp",EDGE,"E15.3");var subQ1=sQuery(id+"F0.wireOp",EDGE,"E15.2");var subQ2=makeQuery(id+"F0.imprint","INTERSECT",VERTEX,{"derivedFrom":[sQuery(id+"F0.wireOp",EDGE,"E14.4"),subQ1,subQ0]});Q46=makeQuery(id+"F0.imprint","IMPRINT",FACE,{"disambiguationData":[TD([[makeQuery(id+"F0.imprint","IMPRINT",EDGE,{"disambiguationData":[TD([[subQ2,1.0]])],"derivedFrom":subQ1}),-1.0]])]});}
            var Q47;
            {var subQ0=sQuery(id+"F0.wireOp",EDGE,"E15.2");var subQ1=sQuery(id+"F0.wireOp",EDGE,"E15.1");var subQ2=makeQuery(id+"F0.imprint","INTERSECT",VERTEX,{"derivedFrom":[sQuery(id+"F0.wireOp",EDGE,"E14.3"),subQ1,subQ0]});Q47=makeQuery(id+"F0.imprint","IMPRINT",FACE,{"disambiguationData":[TD([[makeQuery(id+"F0.imprint","IMPRINT",EDGE,{"disambiguationData":[TD([[subQ2,1.0]])],"derivedFrom":subQ1}),-1.0]])]});}
            extrude(context, id + "F1", {"entities" : qUnion([Q0, Q1, Q2, Q3, Q4, Q5, Q6, Q7, Q8, Q9, Q10, Q11, Q12, Q13, Q14, Q15, Q16, Q17, Q18, Q19, Q20, Q21, Q22, Q23, Q24, Q25, Q26, Q27, Q28, Q29, Q30, Q31, Q32, Q33, Q34, Q35, Q36, Q37, Q38, Q39, Q40, Q41, Q42, Q43, Q44, Q45, Q46, Q47]), "depth" : 25.4 * mm});
        }
    });
